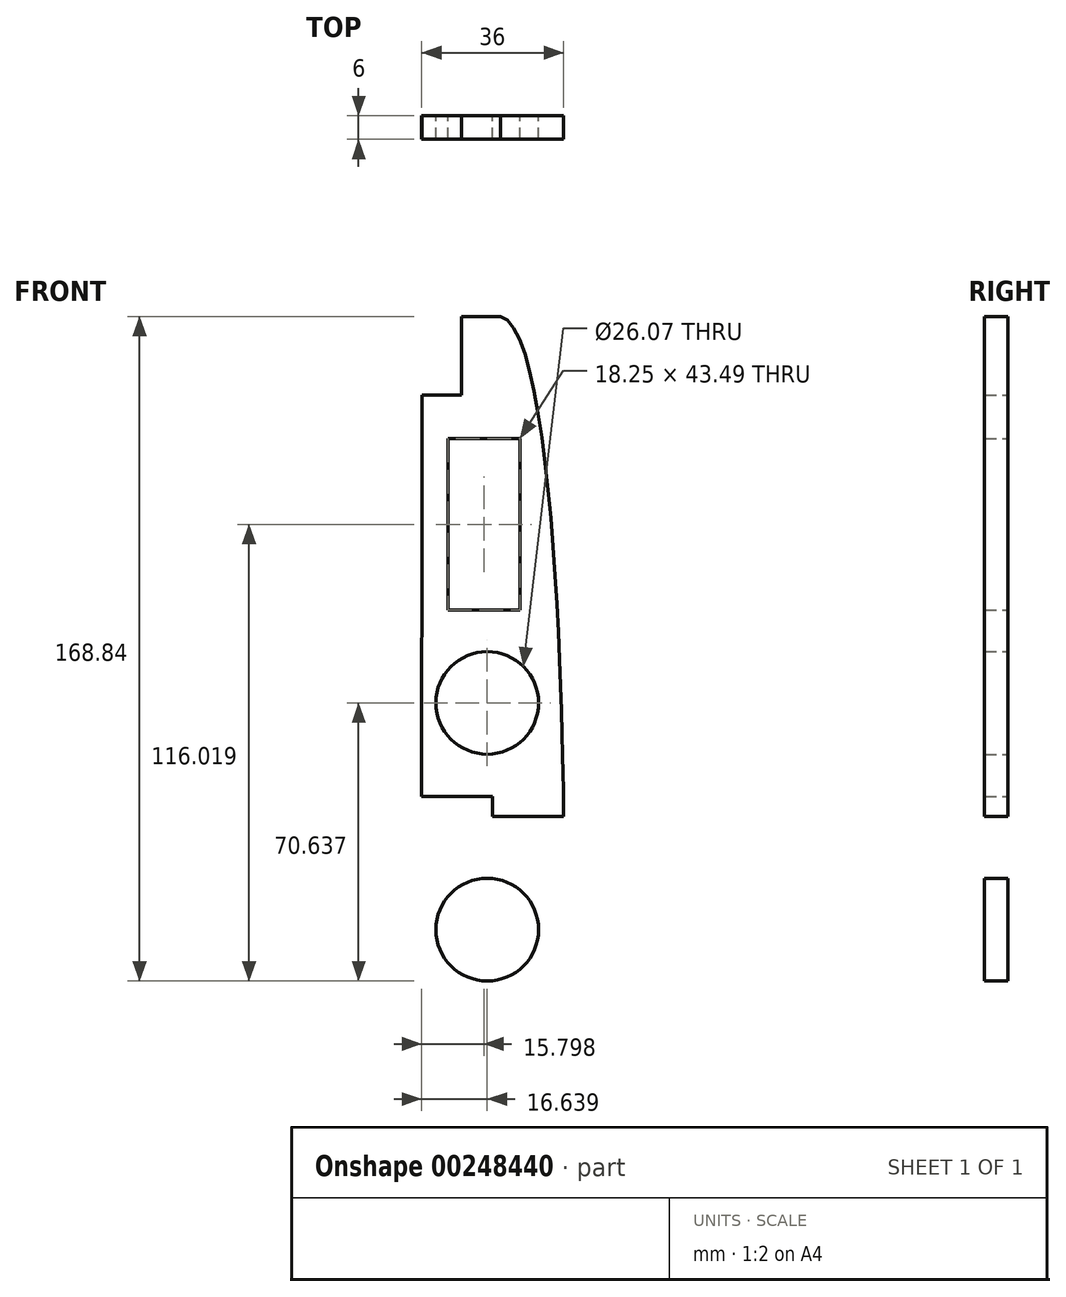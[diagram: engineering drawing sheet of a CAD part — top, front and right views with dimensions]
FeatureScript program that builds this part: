
annotation { "Feature Type Name" : "Feature", "Feature Type Description" : "" }
export const myFeature = defineFeature(function(context is Context, id is Id, definition is map)
    precondition{}
    {
        {
            var Q0;
            Q0=qCreatedBy(makeId("Front.planeOp"),FACE);
            var sketch = newSketch(context, id + "F0", { "sketchPlane" : qUnion([Q0])});
            skLineSegment(sketch, "E0.bottom", {"start": v(121.14, 103.6) * mm, "end": v(95.26, 103.6) * mm});
            skLineSegment(sketch, "E0.top", {"start": v(121.14, -23.4) * mm, "end": v(85.14, -23.4) * mm});
            skLineSegment(sketch, "E0.left", {"start": v(121.14, 103.6) * mm, "end": v(121.14, -23.4) * mm});
            skFitSpline(sketch, "E1", {"points": [v(105.14, 103.6) * mm, v(121.14, -23.4) * mm], "startDerivative": vector(48, -11.4) * mm, "endDerivative": vector(-0.42, 27.38) * mm});
            skCircle(sketch, "E2", {"center": v(101.78, 5.4) * mm, "radius": 13.03 * mm});
            skFitSpline(sketch, "E3.MirrorCS", {"points": [v(105.14, -150.4) * mm, v(121.14, -23.4) * mm], "startDerivative": vector(48, 11.4) * mm, "endDerivative": vector(-0.42, -27.38) * mm});
            skCircle(sketch, "E4.MirrorC", {"center": v(101.78, -52.2) * mm, "radius": 13.03 * mm});
            skLineSegment(sketch, "E5.MirrorCS", {"start": v(121.14, -150.4) * mm, "end": v(121.14, -23.4) * mm});
            skLineSegment(sketch, "E6", {"start": v(103.14, -23.4) * mm, "end": v(103.14, -18.4) * mm});
            skLineSegment(sketch, "E7", {"start": v(103.14, -23.4) * mm, "end": v(103.14, -28.4) * mm});
            skLineSegment(sketch, "E8", {"start": v(103.14, -18.4) * mm, "end": v(85.14, -18.4) * mm});
            skLineSegment(sketch, "E9", {"start": v(103.14, -28.4) * mm, "end": v(85.14, -28.4) * mm});
            skLineSegment(sketch, "E10", {"start": v(95.26, 103.6) * mm, "end": v(95.26, 83.6) * mm});
            skLineSegment(sketch, "E11", {"start": v(95.26, 83.6) * mm, "end": v(85.26, 83.6) * mm});
            skLineSegment(sketch, "E12", {"start": v(85.26, 83.6) * mm, "end": v(85.26, 62.45) * mm});
            skLineSegment(sketch, "E13", {"start": v(85.26, 62.45) * mm, "end": v(85.14, -18.4) * mm});
            skLineSegment(sketch, "E14.bottom", {"start": v(110.06, 72.53) * mm, "end": v(91.81, 72.53) * mm});
            skLineSegment(sketch, "E14.top", {"start": v(110.06, 29.03) * mm, "end": v(91.81, 29.03) * mm});
            skLineSegment(sketch, "E14.left", {"start": v(110.06, 72.53) * mm, "end": v(110.06, 29.03) * mm});
            skLineSegment(sketch, "E14.right", {"start": v(91.81, 72.53) * mm, "end": v(91.81, 29.03) * mm});
            skLineSegment(sketch, "E15.MirrorCS", {"start": v(91.81, -119.33) * mm, "end": v(91.81, -75.84) * mm});
            skLineSegment(sketch, "E16.MirrorCS", {"start": v(110.06, -119.33) * mm, "end": v(91.81, -119.33) * mm});
            skLineSegment(sketch, "E17.MirrorCS", {"start": v(110.06, -119.33) * mm, "end": v(110.06, -75.84) * mm});
            skLineSegment(sketch, "E18.MirrorCS", {"start": v(110.06, -75.84) * mm, "end": v(91.81, -75.84) * mm});
            skLineSegment(sketch, "E19.MirrorCS", {"start": v(95.26, -150.4) * mm, "end": v(95.26, -150.4) * mm});
            skLineSegment(sketch, "E20.MirrorCS", {"start": v(95.26, -130.4) * mm, "end": v(85.26, -130.4) * mm});
            skLineSegment(sketch, "E21", {"start": v(85.26, -130.4) * mm, "end": v(85.26, -130.4) * mm});
            skLineSegment(sketch, "E22", {"start": v(95.26, -150.4) * mm, "end": v(95.26, -130.4) * mm});
            skLineSegment(sketch, "E23", {"start": v(95.26, -150.4) * mm, "end": v(121.14, -150.4) * mm});
            skLineSegment(sketch, "E24", {"start": v(85.26, -130.4) * mm, "end": v(85.14, -28.4) * mm});
            skSolve(sketch);
        }
        {
            var Q0;
            Q0=makeQuery(id+"F0.imprint","IMPRINT",FACE,{"disambiguationData":[TD([[makeQuery(id+"F0.imprint","IMPRINT",EDGE,{"derivedFrom":sQuery(id+"F0.wireOp",EDGE,"E2")}),-1.0]])]});
            var Q1;
            Q1=makeQuery(id+"F0.imprint","IMPRINT",FACE,{"disambiguationData":[TD([[makeQuery(id+"F0.imprint","IMPRINT",EDGE,{"derivedFrom":sQuery(id+"F0.wireOp",EDGE,"007383f6-d1ba-4acf-a4d1-040a27d083ab1.MirrorCS")}),-1.0]])]});
            var Q2;
            Q2=makeQuery(id+"F0.imprint","IMPRINT",FACE,{"disambiguationData":[TD([[makeQuery(id+"F0.imprint","IMPRINT",EDGE,{"derivedFrom":sQuery(id+"F0.wireOp",EDGE,"E4.MirrorC")}),1.0]])]});
            extrude(context, id + "F1", {"entities" : qUnion([Q0, Q1, Q2]), "depth" : 6 * mm});
        }
    });
